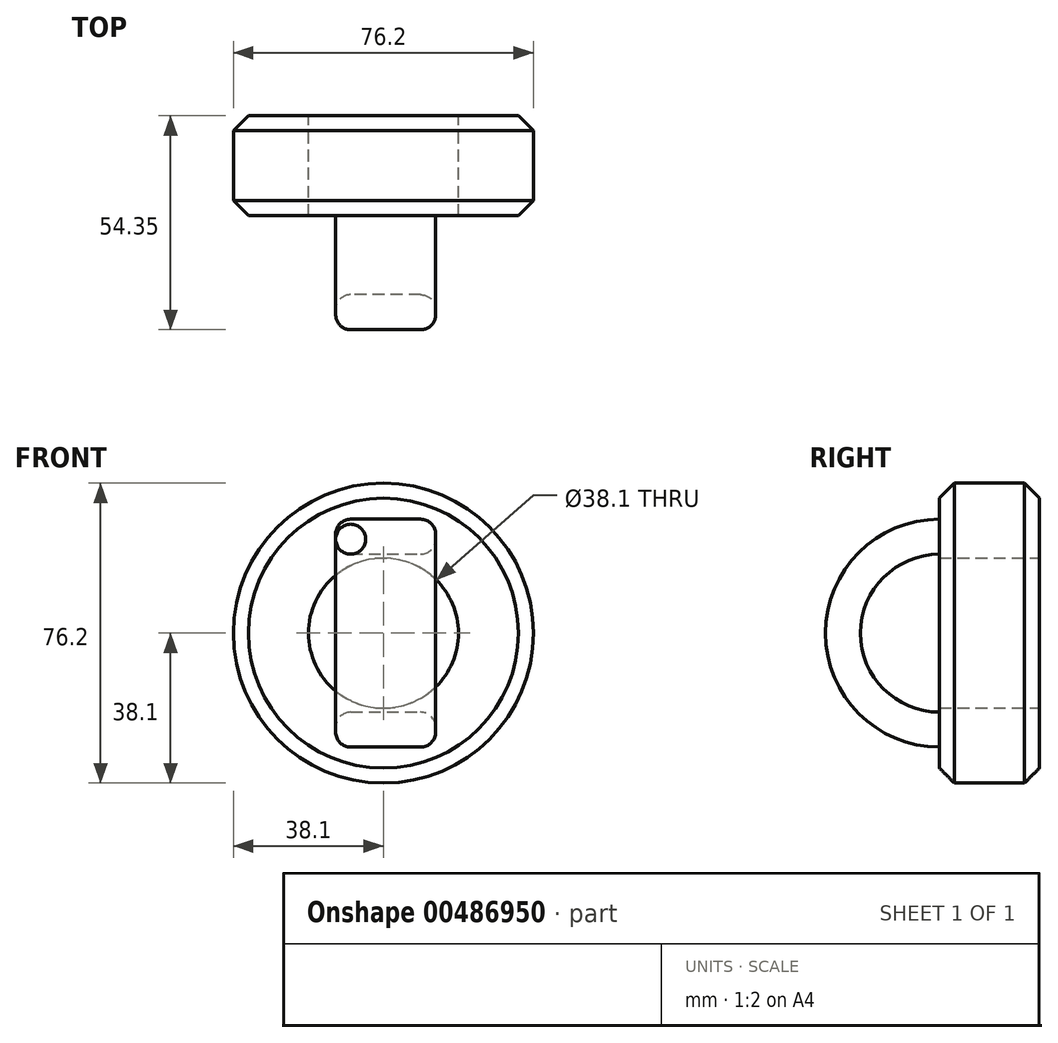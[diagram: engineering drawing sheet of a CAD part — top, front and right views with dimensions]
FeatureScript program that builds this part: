
annotation { "Feature Type Name" : "Feature", "Feature Type Description" : "" }
export const myFeature = defineFeature(function(context is Context, id is Id, definition is map)
    precondition{}
    {
        {
            var Q0;
            Q0=qCreatedBy(makeId("Front.planeOp"),FACE);
            var sketch = newSketch(context, id + "F0", { "sketchPlane" : qUnion([Q0])});
            skCircle(sketch, "E0", {"center": v(0, 0) * mm, "radius": 19.05 * mm});
            skCircle(sketch, "E1", {"center": v(0, 0) * mm, "radius": 38.1 * mm});
            skSolve(sketch);
        }
        {
            var Q0;
            Q0=makeQuery(id+"F0.imprint","IMPRINT",FACE,{"disambiguationData":[TD([[makeQuery(id+"F0.imprint","IMPRINT",EDGE,{"derivedFrom":sQuery(id+"F0.wireOp",EDGE,"E0")}),-1.0]])]});
            extrude(context, id + "F1", {"entities" : qUnion([Q0]), "depth" : 25.4 * mm});
        }
        {
            var Q0;
            Q0=makeQuery(id+"F1.opExtrude","CAP_FACE",FACE,{"disambiguationData":[OSD([sQuery(id+"F0.wireOp",EDGE,"E0"),sQuery(id+"F0.wireOp",EDGE,"E1")])],"isStart":false});
            var sketch = newSketch(context, id + "F2", { "sketchPlane" : qUnion([Q0])});
            skLineSegment(sketch, "E2.bottom", {"start": v(-12.13, 28.95) * mm, "end": v(13.27, 28.95) * mm});
            skLineSegment(sketch, "E2.top", {"start": v(-12.13, 20.06) * mm, "end": v(13.27, 20.06) * mm});
            skLineSegment(sketch, "E2.left", {"start": v(-12.13, 28.95) * mm, "end": v(-12.13, 20.06) * mm});
            skLineSegment(sketch, "E2.right", {"start": v(13.27, 28.95) * mm, "end": v(13.27, 20.06) * mm});
            skLineSegment(sketch, "E3", {"start": v(-72.84, 0) * mm, "end": v(62.08, 0) * mm});
            skSolve(sketch);
        }
        {
            var Q0;
            Q0=makeQuery(id+"F2.imprint","IMPRINT",FACE,{"disambiguationData":[TD([[makeQuery(id+"F2.imprint","IMPRINT",EDGE,{"derivedFrom":sQuery(id+"F2.wireOp",EDGE,"E2.bottom")}),-1.0]])]});
            var Q1;
            Q1=sQuery(id+"F2.wireOp",EDGE,"E3");
            revolve(context, id + "F3", {"operationType" : NewBodyOperationType.ADD, "entities" : qUnion([Q0]), "axis" : qUnion([Q1]), "revolveType" : RevolveType.ONE_DIRECTION, "angle" : 180 * degree});
        }
        {
            var Q0;
            Q0=makeQuery(id+"F3.opRevolve","SWEPT_EDGE",EDGE,{"disambiguationData":[OSD([sQuery(id+"F2.wireOp",EDGE,"E2.bottom"),sQuery(id+"F2.wireOp",EDGE,"E2.right")])]});
            var Q1;
            Q1=makeQuery(id+"F3.opRevolve","SWEPT_EDGE",EDGE,{"disambiguationData":[OSD([sQuery(id+"F2.wireOp",EDGE,"E2.bottom"),sQuery(id+"F2.wireOp",EDGE,"E2.left")])]});
            var Q2;
            Q2=makeQuery(id+"F3.opRevolve","SWEPT_EDGE",EDGE,{"disambiguationData":[OSD([sQuery(id+"F2.wireOp",EDGE,"E2.top"),sQuery(id+"F2.wireOp",EDGE,"E2.right")])]});
            var Q3;
            Q3=makeQuery(id+"F3.opRevolve","SWEPT_EDGE",EDGE,{"disambiguationData":[OSD([sQuery(id+"F2.wireOp",EDGE,"E2.top"),sQuery(id+"F2.wireOp",EDGE,"E2.left")])]});
            fillet(context, id + "F4", {"entities" : qUnion([Q0, Q1, Q2, Q3]), "radius" : 3.8 * mm, "tangentPropagation" : true, "allowEdgeOverflow" : false});
        }
        {
            var Q0;
            Q0=makeQuery(id+"F1.opExtrude","CAP_EDGE",EDGE,{"disambiguationData":[OSD([sQuery(id+"F0.wireOp",EDGE,"E1")])],"isStart":false});
            var Q1;
            Q1=makeQuery(id+"F1.opExtrude","CAP_EDGE",EDGE,{"disambiguationData":[OSD([sQuery(id+"F0.wireOp",EDGE,"E1")])],"isStart":true});
            chamfer(context, id + "F5", {"entities" : qUnion([Q0, Q1]), "width" : 3.8 * mm, "tangentPropagation" : true});
        }
    });
